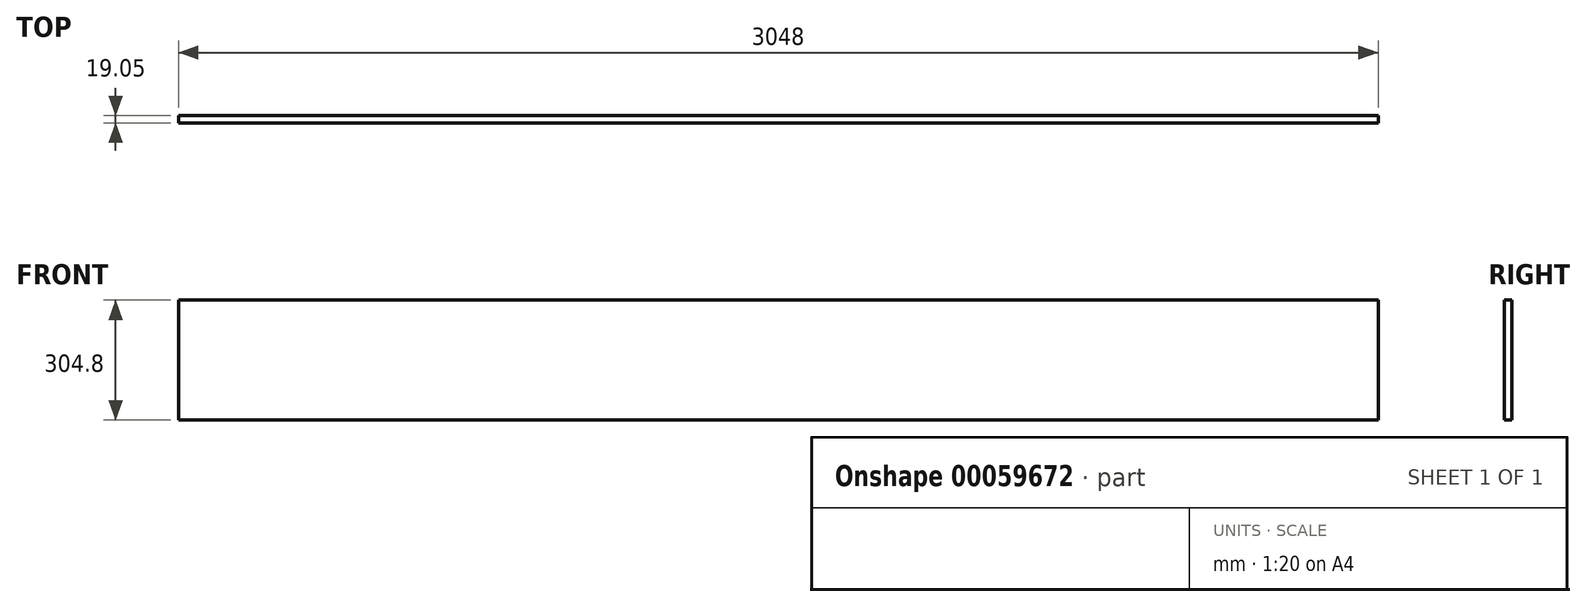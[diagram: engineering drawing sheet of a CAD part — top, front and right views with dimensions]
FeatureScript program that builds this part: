
annotation { "Feature Type Name" : "Feature", "Feature Type Description" : "" }
export const myFeature = defineFeature(function(context is Context, id is Id, definition is map)
    precondition{}
    {
        {
            var Q0;
            Q0=qCreatedBy(makeId("Front.planeOp"),FACE);
            var sketch = newSketch(context, id + "F0", { "sketchPlane" : qUnion([Q0])});
            skLineSegment(sketch, "E0.bottom", {"start": v(0, 0) * mm, "end": v(3048, 0) * mm});
            skLineSegment(sketch, "E0.top", {"start": v(0, 304.8) * mm, "end": v(3048, 304.8) * mm});
            skLineSegment(sketch, "E0.left", {"start": v(0, 0) * mm, "end": v(0, 304.8) * mm});
            skLineSegment(sketch, "E0.right", {"start": v(3048, 0) * mm, "end": v(3048, 304.8) * mm});
            skSolve(sketch);
        }
        {
            var Q0;
            Q0=makeQuery(id+"F0.imprint","IMPRINT",FACE,{"disambiguationData":[TD([[makeQuery(id+"F0.imprint","IMPRINT",EDGE,{"derivedFrom":sQuery(id+"F0.wireOp",EDGE,"E0.bottom")}),1.0]])]});
            extrude(context, id + "F1", {"entities" : qUnion([Q0]), "depth" : 19.05 * mm});
        }
    });
